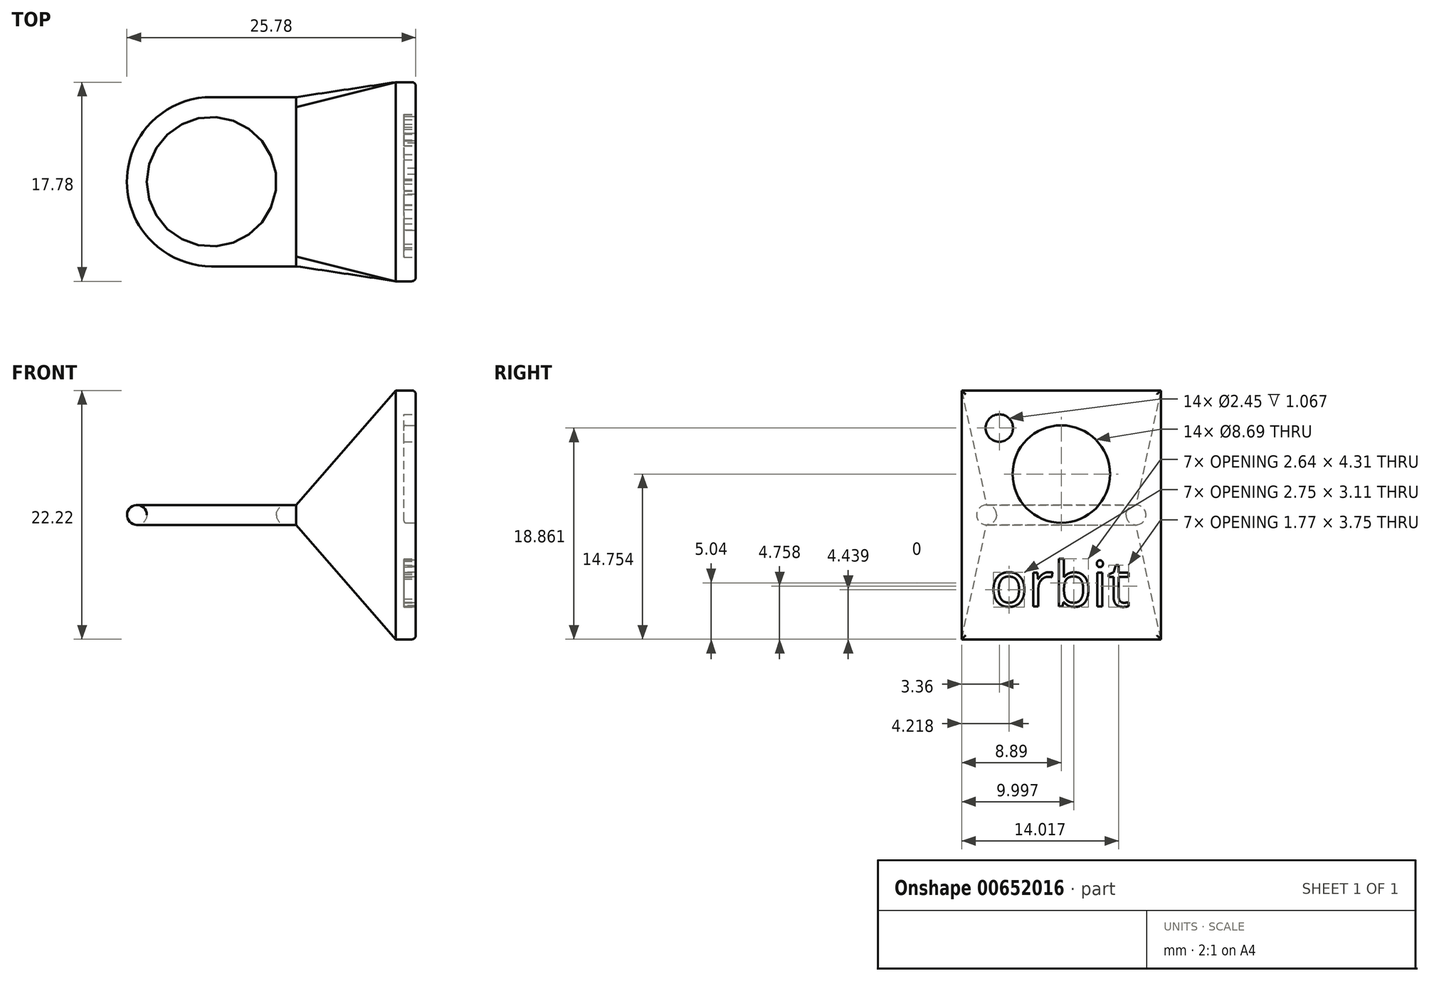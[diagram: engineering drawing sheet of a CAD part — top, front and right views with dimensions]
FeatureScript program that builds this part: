
annotation { "Feature Type Name" : "Feature", "Feature Type Description" : "" }
export const myFeature = defineFeature(function(context is Context, id is Id, definition is map)
    precondition{}
    {
        {
            var Q0;
            Q0=qCreatedBy(makeId("Top.planeOp"),FACE);
            var sketch = newSketch(context, id + "F0", { "sketchPlane" : qUnion([Q0])});
            skCircle(sketch, "E0", {"center": v(0, 0) * mm, "radius": 8.26 * mm});
            skCircle(sketch, "E1.0", {"center": v(0, 0) * mm, "radius": 10.8 * mm});
            skLineSegment(sketch, "E2", {"start": v(0, -10.8) * mm, "end": v(28.84, -10.8) * mm});
            skLineSegment(sketch, "E3", {"start": v(0, 10.8) * mm, "end": v(27.85, 10.8) * mm});
            skLineSegment(sketch, "E4", {"start": v(10.8, 0) * mm, "end": v(10.8, 10.8) * mm});
            skLineSegment(sketch, "E5", {"start": v(10.8, 10.8) * mm, "end": v(10.8, -10.8) * mm});
            skSolve(sketch);
        }
        {
            var Q0;
            Q0=qSketchRegion(id+"F0",true);
            extrude(context, id + "F1", {"entities" : qUnion([Q0]), "depth" : 2.54 * mm, "offsetDistance" : 25.4 * mm});
        }
        {
            var Q0;
            Q0=makeQuery(id+"F1.opExtrude","CAP_EDGE",EDGE,{"disambiguationData":[OSD([sQuery(id+"F0.wireOp",EDGE,"E0")])],"isStart":false});
            var Q1;
            Q1=makeQuery(id+"F1.opExtrude","CAP_EDGE",EDGE,{"disambiguationData":[OSD([sQuery(id+"F0.wireOp",EDGE,"E0")])],"isStart":true});
            var Q2;
            Q2=makeQuery(id+"F1.opExtrude","CAP_EDGE",EDGE,{"disambiguationData":[OSD([sQuery(id+"F0.wireOp",EDGE,"E1.0")])],"isStart":false});
            var Q3;
            Q3=makeQuery(id+"F1.opExtrude","CAP_EDGE",EDGE,{"disambiguationData":[OSD([sQuery(id+"F0.wireOp",EDGE,"E1.0")])],"isStart":true});
            fillet(context, id + "F2", {"entities" : qUnion([Q0, Q1, Q2, Q3]), "radius" : 1.27 * mm, "tangentPropagation" : true, "allowEdgeOverflow" : false});
        }
        {
            var Q0;
            Q0=makeQuery(id+"F1.opExtrude","SWEPT_FACE",FACE,{"disambiguationData":[OSD([sQuery(id+"F0.wireOp",EDGE,"E5")])]});
            cPlane(context, id + "F3", {"entities" : qUnion([Q0]), "cplaneType" : CPlaneType.OFFSET, "offset" : 12.7 * mm, "width" : 152.4 * mm, "height" : 152.4 * mm});
        }
        {
            var Q0;
            Q0=qCreatedBy(id+"F3.planeOp",FACE);
            var sketch = newSketch(context, id + "F4", { "sketchPlane" : qUnion([Q0])});
            skLineSegment(sketch, "E6", {"start": v(0, 0) * mm, "end": v(0, 2.54) * mm});
            skLineSegment(sketch, "E7.bottom", {"start": v(-12.7, 17.15) * mm, "end": v(12.7, 17.15) * mm});
            skLineSegment(sketch, "E7.top", {"start": v(-12.7, -14.6) * mm, "end": v(12.7, -14.6) * mm});
            skLineSegment(sketch, "E7.left", {"start": v(-12.7, 17.15) * mm, "end": v(-12.7, -14.6) * mm});
            skLineSegment(sketch, "E7.right", {"start": v(12.7, 17.15) * mm, "end": v(12.7, -14.6) * mm});
            skPoint(sketch, "E7.middle", {"position": v(0, 1.27) * mm});
            skSolve(sketch);
        }
        {
            var Q0;
            Q0=qSketchRegion(id+"F4",true);
            extrude(context, id + "F5", {"entities" : qUnion([Q0]), "depth" : 2.54 * mm, "offsetDistance" : 25.4 * mm});
        }
        {
            var Q0;
            Q0=makeQuery(id+"F5.opExtrude","CAP_FACE",FACE,{"disambiguationData":[OSD([sQuery(id+"F4.wireOp",EDGE,"E7.bottom"),sQuery(id+"F4.wireOp",EDGE,"E7.top"),sQuery(id+"F4.wireOp",EDGE,"E7.left"),sQuery(id+"F4.wireOp",EDGE,"E7.right")])],"isStart":true});
            var Q1;
            Q1=makeQuery(id+"F1.opExtrude","SWEPT_FACE",FACE,{"disambiguationData":[OSD([sQuery(id+"F0.wireOp",EDGE,"E5")])]});
            loft(context, id + "F6", {"sheetProfilesArray" : [{ "sheetProfileEntities" : qUnion([Q0]) }, { "sheetProfileEntities" : qUnion([Q1]) }]});
        }
        {
            var Q0;
            Q0=makeQuery(id+"F5.opExtrude","CAP_EDGE",EDGE,{"disambiguationData":[OSD([sQuery(id+"F4.wireOp",EDGE,"E7.right")])],"isStart":false});
            var Q1;
            Q1=makeQuery(id+"F5.opExtrude","CAP_EDGE",EDGE,{"disambiguationData":[OSD([sQuery(id+"F4.wireOp",EDGE,"E7.bottom")])],"isStart":false});
            var Q2;
            Q2=makeQuery(id+"F5.opExtrude","CAP_EDGE",EDGE,{"disambiguationData":[OSD([sQuery(id+"F4.wireOp",EDGE,"E7.top")])],"isStart":false});
            var Q3;
            Q3=makeQuery(id+"F5.opExtrude","CAP_EDGE",EDGE,{"disambiguationData":[OSD([sQuery(id+"F4.wireOp",EDGE,"E7.left")])],"isStart":false});
            fillet(context, id + "F7", {"entities" : qUnion([Q0, Q1, Q2, Q3]), "radius" : 0.5 * mm, "tangentPropagation" : true, "allowEdgeOverflow" : false});
        }
        {
            var Q0;
            Q0=makeQuery(id+"F5.opExtrude","CAP_FACE",FACE,{"disambiguationData":[OSD([sQuery(id+"F4.wireOp",EDGE,"E7.bottom"),sQuery(id+"F4.wireOp",EDGE,"E7.top"),sQuery(id+"F4.wireOp",EDGE,"E7.left"),sQuery(id+"F4.wireOp",EDGE,"E7.right")])],"isStart":false});
            var sketch = newSketch(context, id + "F8", { "sketchPlane" : qUnion([Q0])});
            skLineSegment(sketch, "E8", {"start": v(0, -12.57) * mm, "end": v(0, 16.64) * mm});
            skCircle(sketch, "E9", {"center": v(0, 6.48) * mm, "radius": 6.21 * mm});
            skCircle(sketch, "E10", {"center": v(-7.9, 12.34) * mm, "radius": 1.75 * mm});
            skText(sketch, "E11", { "text": "orbit", "fontName": "OpenSans-Regular.ttf"});
            skLineSegment(sketch, "E12.MirrorCS", {"start": v(0, 12.57) * mm, "end": v(0, -16.64) * mm});
            const initialGuessF8  = {"E11": [-0.00909, -0.0104, 1, 0, 0.00576]};
            skSetInitialGuess(sketch, initialGuessF8);
            skSolve(sketch);
        }
        {
            var Q0;
            Q0=qSketchRegion(id+"F8",true);
            extrude(context, id + "F9", {"entities" : qUnion([Q0]), "operationType" : NewBodyOperationType.REMOVE, "oppositeDirection" : true, "depth" : 1.52 * mm, "offsetDistance" : 25.4 * mm});
        }
        {
            var Q0;
            Q0=makeQuery(id+"F9.boolean.opBoolean","COPY",EDGE,{"derivedFrom":makeQuery(id+"F9.opExtrude","CAP_EDGE",EDGE,{"disambiguationData":[OSD([sQuery(id+"F8.wireOp",EDGE,"E9")])],"isStart":false})});
            fillet(context, id + "F10", {"entities" : qUnion([Q0]), "radius" : 0.25 * mm, "tangentPropagation" : true, "allowEdgeOverflow" : false});
        }
        {
            var Q0;
            Q0=makeQuery(id+"F1.opExtrude","SWEPT_BODY",BODY,{"disambiguationData":[OSD([sQuery(id+"F0.wireOp",EDGE,"E0"),sQuery(id+"F0.wireOp",EDGE,"E1.0"),sQuery(id+"F0.wireOp",EDGE,"E2"),sQuery(id+"F0.wireOp",EDGE,"E3"),sQuery(id+"F0.wireOp",EDGE,"E5")])]});
            var Q1;
            Q1=makeQuery(id+"F5.opExtrude","SWEPT_BODY",BODY,{"disambiguationData":[OSD([sQuery(id+"F4.wireOp",EDGE,"E7.bottom"),sQuery(id+"F4.wireOp",EDGE,"E7.top"),sQuery(id+"F4.wireOp",EDGE,"E7.left"),sQuery(id+"F4.wireOp",EDGE,"E7.right")])]});
            var Q2;
            Q2=makeQuery(id+"F6.opLoft","SWEPT_BODY",BODY,{"disambiguationData":[OSD([sQuery(id+"F0.wireOp",EDGE,"E5"),sQuery(id+"F4.wireOp",EDGE,"E7.bottom"),sQuery(id+"F4.wireOp",EDGE,"E7.top"),sQuery(id+"F4.wireOp",EDGE,"E7.left"),sQuery(id+"F4.wireOp",EDGE,"E7.right")])]});
            var Q3;
            Q3=qCreatedBy(makeId("Origin.pointOp"),VERTEX);
            transform(context, id + "F11", {"entities" : qUnion([Q0, Q1, Q2]), "transformType" : TransformType.SCALE_UNIFORMLY, "scale" : .7, "scalePoint" : qUnion([Q3]), "makeCopy" : false});
        }
    });
